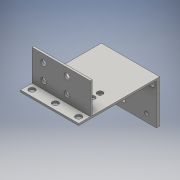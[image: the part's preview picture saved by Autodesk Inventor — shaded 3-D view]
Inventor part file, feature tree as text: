
AUTODESK INVENTOR PART (.ipt)
format: ipt  version: 2016 (Build 200138000, 138)  size: 199,168 bytes
history: native  units: mm
features: sketch x8, hole x6, extrude x3
ambient origin geometry x8: Origin, YZ Plane, XZ Plane, XY Plane, X Axis, Y Axis, Z Axis, Center Point
bodies: Solid1 (feature_tree)
feature tree (17):
  extrude  "Extrusion1"  Depth=31.5mm
  extrude  "Extrusion2"  Depth=45.0mm
  hole  "Hole1"  [1 undecoded]
  hole  "Hole2"  [1 undecoded]
  extrude  "Extrusion3"  Depth=4.6mm
  hole  "Hole3"  [1 undecoded]
  hole  "Hole4"  [1 undecoded]
  hole  "Hole5"  [1 undecoded]
  hole  "Hole6"  [1 undecoded]
  sketch  "Sketch1"  dims[d0=45.0mm d1=31.5mm]
  sketch  "Sketch2"  dims[d2=2.5mm d3=0.0mm d4=45.0mm]
  sketch  "Sketch4"  dims[d5=1.5mm d6=60.0mm d7=2.5mm d8=0.0mm d9=0.0mm]
  sketch  "Sketch5"  dims[d10=4.6mm d11=3.5mm]
  sketch  "Sketch6"  dims[d12=3.5mm d16=4.6mm]
  sketch  "Sketch7"  dims[d17=3.5mm d18=3.5mm]
  sketch  "Sketch9"  dims[d19=4.6mm d20=3.5mm]
  sketch  "Sketch10"  dims[d21=3.5mm d22=4.6mm d23=6.0mm d24=4.0mm d25=2.0mm d26=90.0deg d27=8.0mm d28=20.594885mm d29=4.3mm d30=4.5mm d31=4.5mm d32=4.3mm d33=4.5mm d34=4.5mm d35=4.3mm d36=4.6mm d37=6.0mm d38=4.0mm d39=2.0mm d40=90.0deg d41=8.0mm d42=20.594885mm d43=4.5mm d44=1.5mm d45=24.0mm d46=0.0mm d47=2.6mm d48=9.0mm d49=12.0mm d50=4.3mm d51=24.0mm d52=4.3mm d53=6.0mm d54=4.3mm d55=6.0mm d56=4.3mm d57=6.0mm d58=4.0mm d59=2.0mm d60=90.0deg d61=8.0mm d62=20.594885mm d66=2.6mm d67=6.0mm d68=4.0mm d69=2.0mm d70=90.0deg d71=8.0mm d72=20.594885mm d73=4.3mm d74=6.0mm d75=9.0mm d76=4.3mm d77=12.0mm d78=4.3mm d79=18.0mm d80=4.3mm d81=4.3mm d82=6.0mm d83=4.0mm d84=2.0mm d85=90.0deg d86=8.0mm d87=20.594885mm d89=2.6mm d91=9.0mm d92=3.0mm d93=6.0mm d94=7.5mm d95=3.0mm d96=18.0mm d97=3.0mm d98=6.0mm d99=4.0mm d100=2.0mm d101=90.0deg d102=8.0mm d103=20.594885mm d104=18.0mm d105=9.0mm]
note: 6 required parameter values undecoded (feature->parameter linkage not recoverable at this tier; creation-order binding heuristic only, values carry confidence <= 0.55)
